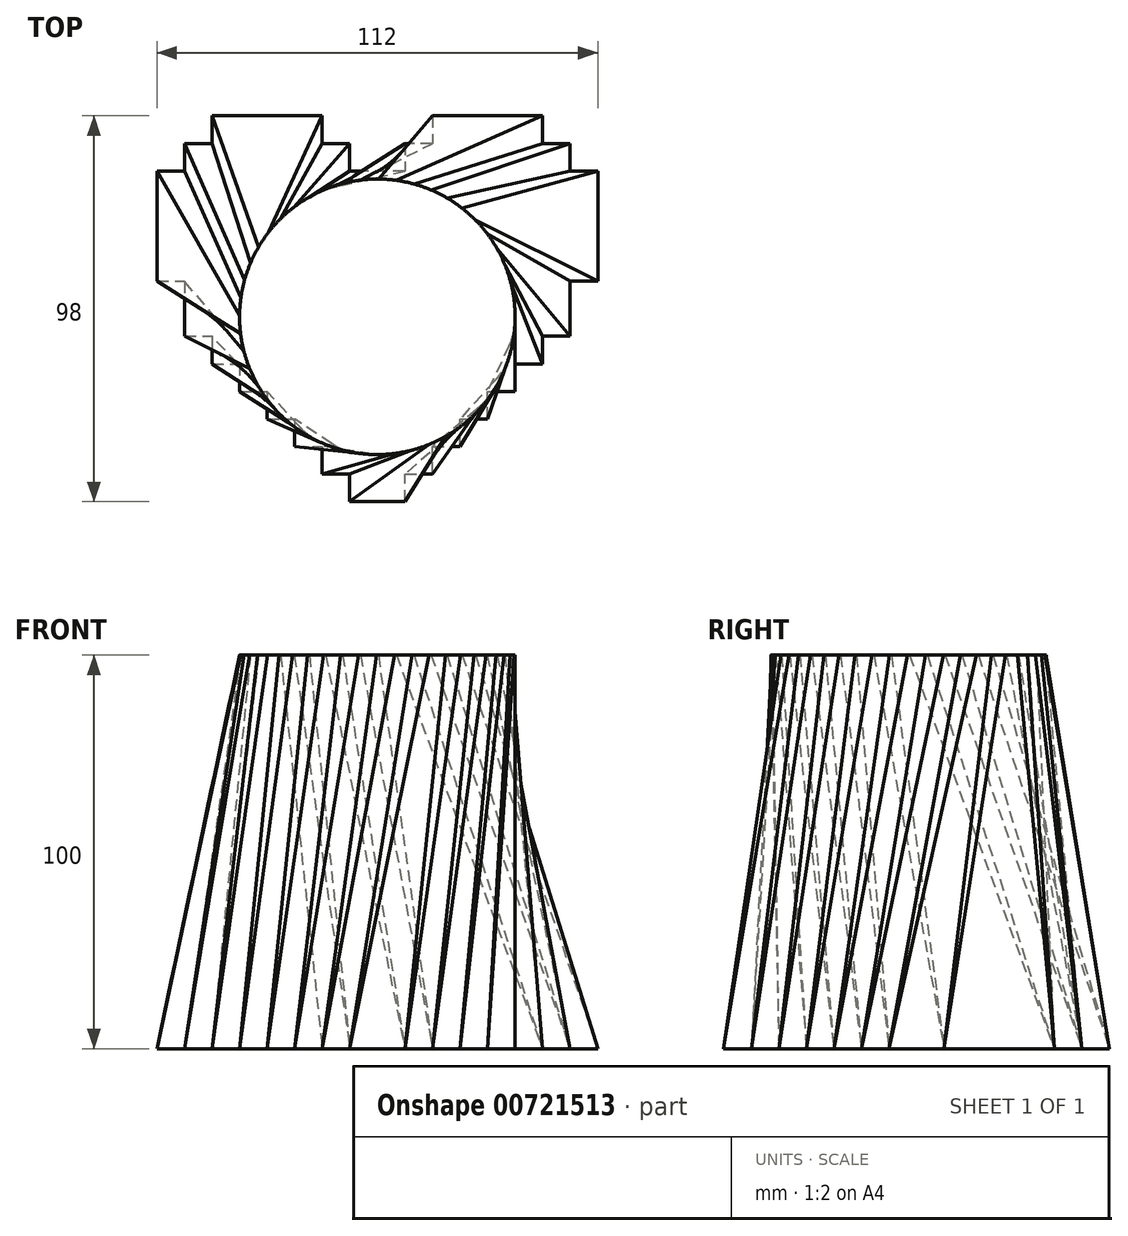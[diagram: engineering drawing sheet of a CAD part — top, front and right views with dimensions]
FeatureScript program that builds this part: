
annotation { "Feature Type Name" : "Feature", "Feature Type Description" : "" }
export const myFeature = defineFeature(function(context is Context, id is Id, definition is map)
    precondition{}
    {
        {
            var Q0;
            Q0=qCreatedBy(makeId("Top.planeOp"),FACE);
            var sketch = newSketch(context, id + "F0", { "sketchPlane" : qUnion([Q0])});
            skLineSegment(sketch, "E0", {"start": v(39.3, 20.05) * mm, "end": v(39.3, 27.05) * mm});
            skLineSegment(sketch, "E1", {"start": v(39.3, 27.05) * mm, "end": v(32.3, 27.05) * mm});
            skLineSegment(sketch, "E2", {"start": v(32.3, 27.05) * mm, "end": v(32.3, 34.05) * mm});
            skLineSegment(sketch, "E3", {"start": v(32.3, 34.05) * mm, "end": v(4.3, 34.05) * mm});
            skLineSegment(sketch, "E4", {"start": v(4.3, 34.05) * mm, "end": v(4.3, 27.05) * mm});
            skLineSegment(sketch, "E5", {"start": v(4.3, 27.05) * mm, "end": v(-2.7, 27.05) * mm});
            skLineSegment(sketch, "E6", {"start": v(-2.7, 27.05) * mm, "end": v(-2.7, 20.05) * mm});
            skLineSegment(sketch, "E7", {"start": v(-2.7, 20.05) * mm, "end": v(-16.7, 20.05) * mm});
            skLineSegment(sketch, "E8", {"start": v(-16.7, 20.05) * mm, "end": v(-16.7, 27.05) * mm});
            skLineSegment(sketch, "E9", {"start": v(-16.7, 27.05) * mm, "end": v(-23.7, 27.05) * mm});
            skLineSegment(sketch, "E10", {"start": v(-23.7, 27.05) * mm, "end": v(-23.7, 34.05) * mm});
            skLineSegment(sketch, "E11", {"start": v(-23.7, 34.05) * mm, "end": v(-51.7, 34.05) * mm});
            skLineSegment(sketch, "E12", {"start": v(-51.7, 34.05) * mm, "end": v(-51.7, 27.05) * mm});
            skLineSegment(sketch, "E13", {"start": v(-51.7, 27.05) * mm, "end": v(-58.7, 27.05) * mm});
            skLineSegment(sketch, "E14", {"start": v(-58.7, 27.05) * mm, "end": v(-58.7, 20.05) * mm});
            skLineSegment(sketch, "E15", {"start": v(-58.7, 20.05) * mm, "end": v(-65.7, 20.05) * mm});
            skLineSegment(sketch, "E16", {"start": v(-65.7, 20.05) * mm, "end": v(-65.7, -7.95) * mm});
            skLineSegment(sketch, "E17", {"start": v(-65.7, -7.95) * mm, "end": v(-58.7, -7.95) * mm});
            skLineSegment(sketch, "E18", {"start": v(-58.7, -7.95) * mm, "end": v(-58.7, -21.95) * mm});
            skLineSegment(sketch, "E19", {"start": v(-58.7, -21.95) * mm, "end": v(-51.7, -21.95) * mm});
            skLineSegment(sketch, "E20", {"start": v(-51.7, -21.95) * mm, "end": v(-51.7, -28.95) * mm});
            skLineSegment(sketch, "E21", {"start": v(-51.7, -28.95) * mm, "end": v(-44.7, -28.95) * mm});
            skLineSegment(sketch, "E22", {"start": v(-44.7, -28.95) * mm, "end": v(-44.7, -35.95) * mm});
            skLineSegment(sketch, "E23", {"start": v(-44.7, -35.95) * mm, "end": v(-37.7, -35.95) * mm});
            skLineSegment(sketch, "E24", {"start": v(-37.7, -35.95) * mm, "end": v(-37.7, -42.95) * mm});
            skLineSegment(sketch, "E25", {"start": v(-37.7, -42.95) * mm, "end": v(-30.7, -42.95) * mm});
            skLineSegment(sketch, "E26", {"start": v(-30.7, -42.95) * mm, "end": v(-30.7, -49.95) * mm});
            skLineSegment(sketch, "E27", {"start": v(-30.7, -49.95) * mm, "end": v(-23.7, -49.95) * mm});
            skLineSegment(sketch, "E28", {"start": v(-23.7, -49.95) * mm, "end": v(-23.7, -56.95) * mm});
            skLineSegment(sketch, "E29", {"start": v(-23.7, -56.95) * mm, "end": v(-16.7, -56.95) * mm});
            skLineSegment(sketch, "E30", {"start": v(-16.7, -56.95) * mm, "end": v(-16.7, -63.95) * mm});
            skLineSegment(sketch, "E31", {"start": v(-16.7, -63.95) * mm, "end": v(-2.7, -63.95) * mm});
            skLineSegment(sketch, "E32", {"start": v(-2.7, -63.95) * mm, "end": v(-2.7, -56.95) * mm});
            skLineSegment(sketch, "E33", {"start": v(-2.7, -56.95) * mm, "end": v(4.3, -56.95) * mm});
            skLineSegment(sketch, "E34", {"start": v(4.3, -56.95) * mm, "end": v(4.3, -49.95) * mm});
            skLineSegment(sketch, "E35", {"start": v(4.3, -49.95) * mm, "end": v(11.3, -49.95) * mm});
            skLineSegment(sketch, "E36", {"start": v(11.3, -49.95) * mm, "end": v(11.3, -42.95) * mm});
            skLineSegment(sketch, "E37", {"start": v(11.3, -42.95) * mm, "end": v(18.3, -42.95) * mm});
            skLineSegment(sketch, "E38", {"start": v(18.3, -42.95) * mm, "end": v(18.3, -35.95) * mm});
            skLineSegment(sketch, "E39", {"start": v(18.3, -35.95) * mm, "end": v(25.3, -35.95) * mm});
            skLineSegment(sketch, "E40", {"start": v(25.3, -35.95) * mm, "end": v(25.3, -28.95) * mm});
            skLineSegment(sketch, "E41", {"start": v(25.3, -28.95) * mm, "end": v(32.3, -28.95) * mm});
            skLineSegment(sketch, "E42", {"start": v(32.3, -28.95) * mm, "end": v(32.3, -21.95) * mm});
            skLineSegment(sketch, "E43", {"start": v(32.3, -21.95) * mm, "end": v(39.3, -21.95) * mm});
            skLineSegment(sketch, "E44", {"start": v(39.3, -21.95) * mm, "end": v(39.3, -7.95) * mm});
            skLineSegment(sketch, "E45", {"start": v(39.3, -7.95) * mm, "end": v(46.3, -7.95) * mm});
            skLineSegment(sketch, "E46", {"start": v(46.3, -7.95) * mm, "end": v(46.3, 20.05) * mm});
            skLineSegment(sketch, "E47", {"start": v(46.3, 20.05) * mm, "end": v(39.3, 20.05) * mm});
            skLineSegment(sketch, "E48", {"start": v(-9.7, 20.05) * mm, "end": v(-9.7, -63.95) * mm, "construction": true});
            skSolve(sketch);
        }
        {
            var Q0;
            Q0=qCreatedBy(makeId("Top.planeOp"),FACE);
            cPlane(context, id + "F1", {"entities" : qUnion([Q0]), "cplaneType" : CPlaneType.OFFSET, "offset" : 100 * mm, "width" : 150 * mm, "height" : 150 * mm});
        }
        {
            var Q0;
            Q0=qCreatedBy(id+"F1.planeOp",FACE);
            var sketch = newSketch(context, id + "F2", { "sketchPlane" : qUnion([Q0])});
            skCircle(sketch, "E49", {"center": v(-9.7, -17) * mm, "radius": 35 * mm});
            skLineSegment(sketch, "E50", {"start": v(-9.7, -17) * mm, "end": v(-9.7, 34.67) * mm, "construction": true});
            skSolve(sketch);
        }
        {
            var Q0;
            Q0=makeQuery(id+"F2.imprint","IMPRINT",FACE,{"disambiguationData":[TD([[makeQuery(id+"F2.imprint","IMPRINT",EDGE,{"derivedFrom":sQuery(id+"F2.wireOp",EDGE,"E49")}),1.0]])]});
            var Q1;
            Q1=makeQuery(id+"F0.imprint","IMPRINT",FACE,{"disambiguationData":[TD([[makeQuery(id+"F0.imprint","IMPRINT",EDGE,{"derivedFrom":sQuery(id+"F0.wireOp",EDGE,"E0")}),1.0]])]});
            loft(context, id + "F3", {"sheetProfilesArray" : [{ "sheetProfileEntities" : qUnion([Q0]) }, { "sheetProfileEntities" : qUnion([Q1]) }]});
        }
    });
